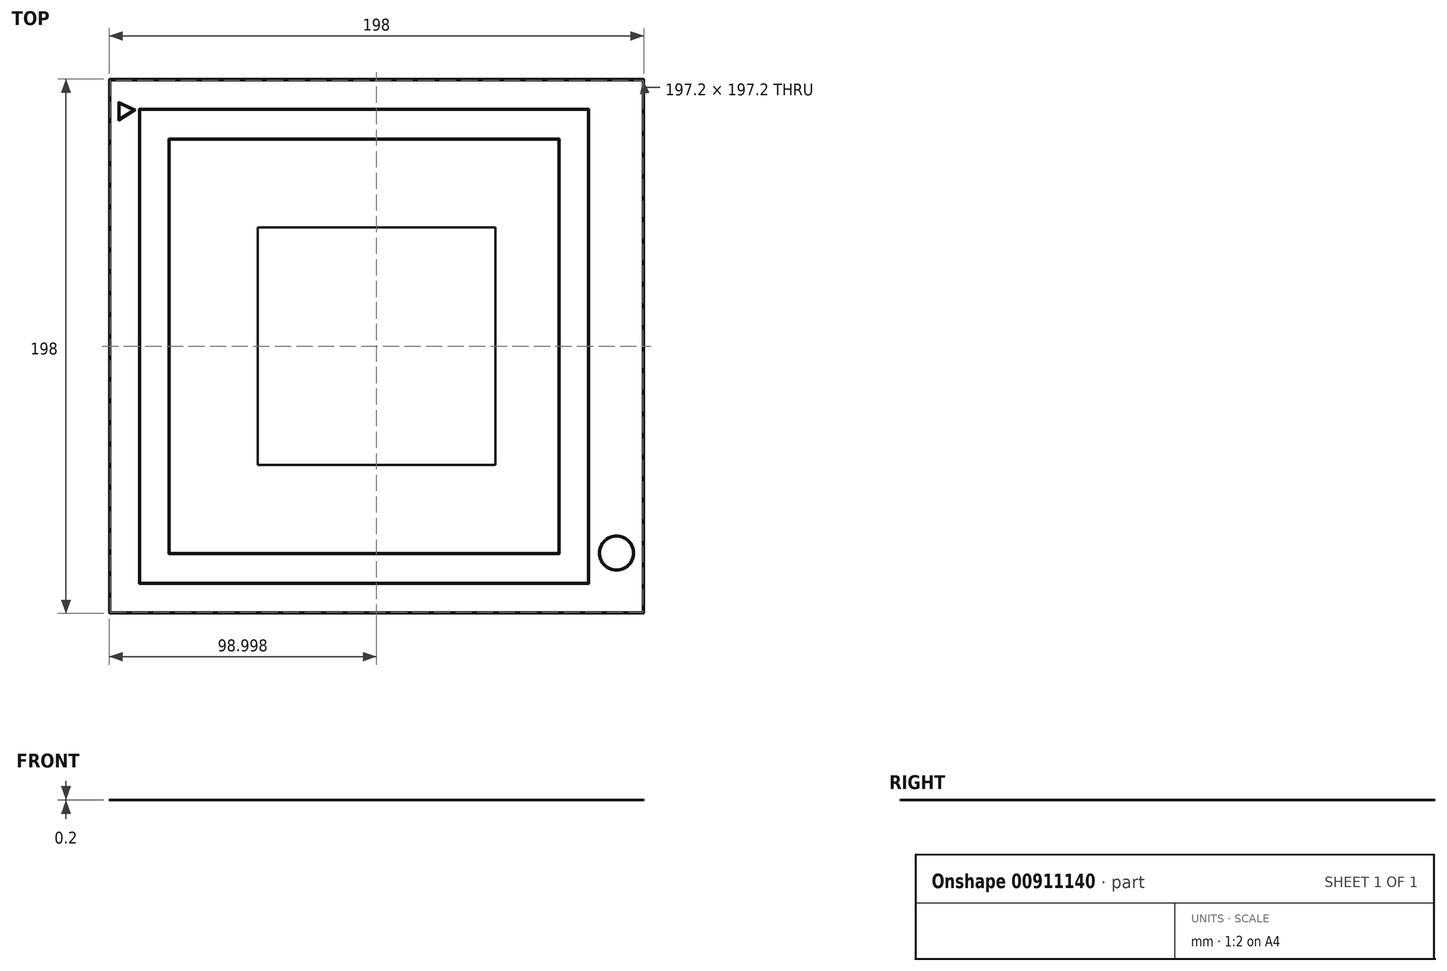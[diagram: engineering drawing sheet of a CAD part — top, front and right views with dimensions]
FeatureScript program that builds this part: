
annotation { "Feature Type Name" : "Feature", "Feature Type Description" : "" }
export const myFeature = defineFeature(function(context is Context, id is Id, definition is map)
    precondition{}
    {
        {
            assignVariable(context, id + "F0", {"name" : "LineHeight", "anyValue" : 0.2});
        }
        {
            var Q0;
            Q0=qCreatedBy(makeId("Top.planeOp"),FACE);
            var sketch = newSketch(context, id + "F1", { "sketchPlane" : qUnion([Q0])});
            skLineSegment(sketch, "E0.bottom", {"start": v(-91.48, 125.86) * mm, "end": v(106.52, 125.86) * mm});
            skLineSegment(sketch, "E0.top", {"start": v(-91.48, -72.14) * mm, "end": v(106.52, -72.14) * mm});
            skLineSegment(sketch, "E0.left", {"start": v(-91.48, 125.86) * mm, "end": v(-91.48, -72.14) * mm});
            skLineSegment(sketch, "E0.right", {"start": v(106.52, 125.86) * mm, "end": v(106.52, -72.14) * mm});
            skLineSegment(sketch, "E1.bottom", {"start": v(-80.48, 114.86) * mm, "end": v(86.23, 114.86) * mm});
            skLineSegment(sketch, "E1.top", {"start": v(-80.48, -61.14) * mm, "end": v(86.23, -61.14) * mm});
            skLineSegment(sketch, "E1.left", {"start": v(-80.48, 114.86) * mm, "end": v(-80.48, -61.14) * mm});
            skLineSegment(sketch, "E1.right", {"start": v(86.23, 114.86) * mm, "end": v(86.23, -61.14) * mm});
            skLineSegment(sketch, "E2.bottom", {"start": v(-69.48, 103.86) * mm, "end": v(75.23, 103.86) * mm});
            skLineSegment(sketch, "E2.top", {"start": v(-69.48, -50.14) * mm, "end": v(75.23, -50.14) * mm});
            skLineSegment(sketch, "E2.left", {"start": v(-69.48, 103.86) * mm, "end": v(-69.48, -50.14) * mm});
            skLineSegment(sketch, "E2.right", {"start": v(75.23, 103.86) * mm, "end": v(75.23, -50.14) * mm});
            skLineSegment(sketch, "E3.bottom", {"start": v(-36.48, 70.86) * mm, "end": v(51.52, 70.86) * mm});
            skLineSegment(sketch, "E3.top", {"start": v(-36.48, -17.14) * mm, "end": v(51.52, -17.14) * mm});
            skLineSegment(sketch, "E3.left", {"start": v(-36.48, 70.86) * mm, "end": v(-36.48, -17.14) * mm});
            skLineSegment(sketch, "E3.right", {"start": v(51.52, 70.86) * mm, "end": v(51.52, -17.14) * mm});
            skLineSegment(sketch, "E4", {"start": v(-88.08, 117.46) * mm, "end": v(-88.08, 110.46) * mm});
            skLineSegment(sketch, "E5", {"start": v(-88.08, 110.46) * mm, "end": v(-81.76, 114.46) * mm});
            skLineSegment(sketch, "E6", {"start": v(-81.76, 114.46) * mm, "end": v(-88.08, 117.46) * mm});
            skCircle(sketch, "E7", {"center": v(96.37, -49.74) * mm, "radius": 6.5 * mm});
            skLineSegment(sketch, "E8", {"start": v(86.23, -49.74) * mm, "end": v(106.52, -49.74) * mm, "construction": true});
            skLineSegment(sketch, "E9", {"start": v(-91.08, 125.46) * mm, "end": v(106.12, 125.46) * mm});
            skLineSegment(sketch, "E10", {"start": v(106.12, 125.46) * mm, "end": v(106.12, -71.74) * mm});
            skLineSegment(sketch, "E11", {"start": v(106.12, -71.74) * mm, "end": v(-91.08, -71.74) * mm});
            skLineSegment(sketch, "E12", {"start": v(-91.08, -71.74) * mm, "end": v(-91.08, 125.46) * mm});
            skLineSegment(sketch, "E13", {"start": v(-80.08, 114.46) * mm, "end": v(85.83, 114.46) * mm});
            skLineSegment(sketch, "E14", {"start": v(85.83, 114.46) * mm, "end": v(85.83, -60.74) * mm});
            skLineSegment(sketch, "E15", {"start": v(85.83, -60.74) * mm, "end": v(-80.08, -60.74) * mm});
            skLineSegment(sketch, "E16", {"start": v(-80.08, -60.74) * mm, "end": v(-80.08, 114.46) * mm});
            skLineSegment(sketch, "E17", {"start": v(-69.08, 103.46) * mm, "end": v(74.83, 103.46) * mm});
            skLineSegment(sketch, "E18", {"start": v(74.83, 103.46) * mm, "end": v(74.83, -49.74) * mm});
            skLineSegment(sketch, "E19", {"start": v(74.83, -49.74) * mm, "end": v(-69.08, -49.74) * mm});
            skLineSegment(sketch, "E20", {"start": v(-69.08, -49.74) * mm, "end": v(-69.08, 103.46) * mm});
            skCircle(sketch, "E21", {"center": v(96.37, -49.74) * mm, "radius": 6.1 * mm});
            skLineSegment(sketch, "E22", {"start": v(-87.68, 116.83) * mm, "end": v(-82.59, 114.41) * mm});
            skPoint(sketch, "E22.startSnap0", {"position": v(-85.61, 116.83) * mm});
            skLineSegment(sketch, "E23", {"start": v(-82.59, 114.41) * mm, "end": v(-87.68, 111.19) * mm});
            skLineSegment(sketch, "E24", {"start": v(-87.68, 111.19) * mm, "end": v(-87.68, 116.83) * mm});
            skSolve(sketch);
        }
        {
            var Q0;
            Q0=makeQuery(id+"F1.imprint","IMPRINT",FACE,{"disambiguationData":[TD([[makeQuery(id+"F1.imprint","IMPRINT",EDGE,{"derivedFrom":sQuery(id+"F1.wireOp",EDGE,"E0.bottom")}),-1.0]])]});
            var Q1;
            Q1=makeQuery(id+"F1.imprint","IMPRINT",FACE,{"disambiguationData":[TD([[makeQuery(id+"F1.imprint","IMPRINT",EDGE,{"derivedFrom":sQuery(id+"F1.wireOp",EDGE,"E1.bottom")}),-1.0]])]});
            var Q2;
            Q2=makeQuery(id+"F1.imprint","IMPRINT",FACE,{"disambiguationData":[TD([[makeQuery(id+"F1.imprint","IMPRINT",EDGE,{"derivedFrom":sQuery(id+"F1.wireOp",EDGE,"E2.bottom")}),-1.0]])]});
            var Q3;
            Q3=makeQuery(id+"F1.imprint","IMPRINT",FACE,{"disambiguationData":[TD([[makeQuery(id+"F1.imprint","IMPRINT",EDGE,{"derivedFrom":sQuery(id+"F1.wireOp",EDGE,"E7")}),1.0]])]});
            var Q4;
            Q4=makeQuery(id+"F1.imprint","IMPRINT",FACE,{"disambiguationData":[TD([[makeQuery(id+"F1.imprint","IMPRINT",EDGE,{"derivedFrom":sQuery(id+"F1.wireOp",EDGE,"E3.bottom")}),-1.0]])]});
            var Q5;
            Q5=makeQuery(id+"F1.imprint","IMPRINT",FACE,{"disambiguationData":[TD([[makeQuery(id+"F1.imprint","IMPRINT",EDGE,{"derivedFrom":sQuery(id+"F1.wireOp",EDGE,"E4")}),1.0]])]});
            extrude(context, id + "F2", {"entities" : qUnion([Q0, Q1, Q2, Q3, Q4, Q5]), "depth" : (getVariable(context, 'LineHeight')) * mm, "offsetDistance" : 25 * mm});
        }
    });
